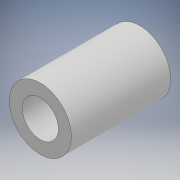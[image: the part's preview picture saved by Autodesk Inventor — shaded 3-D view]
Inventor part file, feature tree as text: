
AUTODESK INVENTOR PART (.ipt)
format: ipt  version: 2017.3 (Build 213256000, 256)  size: 95,232 bytes
history: native  units: mm
features: extrude x1, sketch x1
ambient origin geometry x8: Origin, YZ Plane, XZ Plane, XY Plane, X Axis, Y Axis, Z Axis, Center Point
bodies: Solid1 (feature_tree)
feature tree (2):
  extrude  "Extrusion1"  Depth=8.5mm
  sketch  "Sketch1"  dims[d0=3.1mm d1=1.1mm d2=8.5mm d3=0.0mm]
